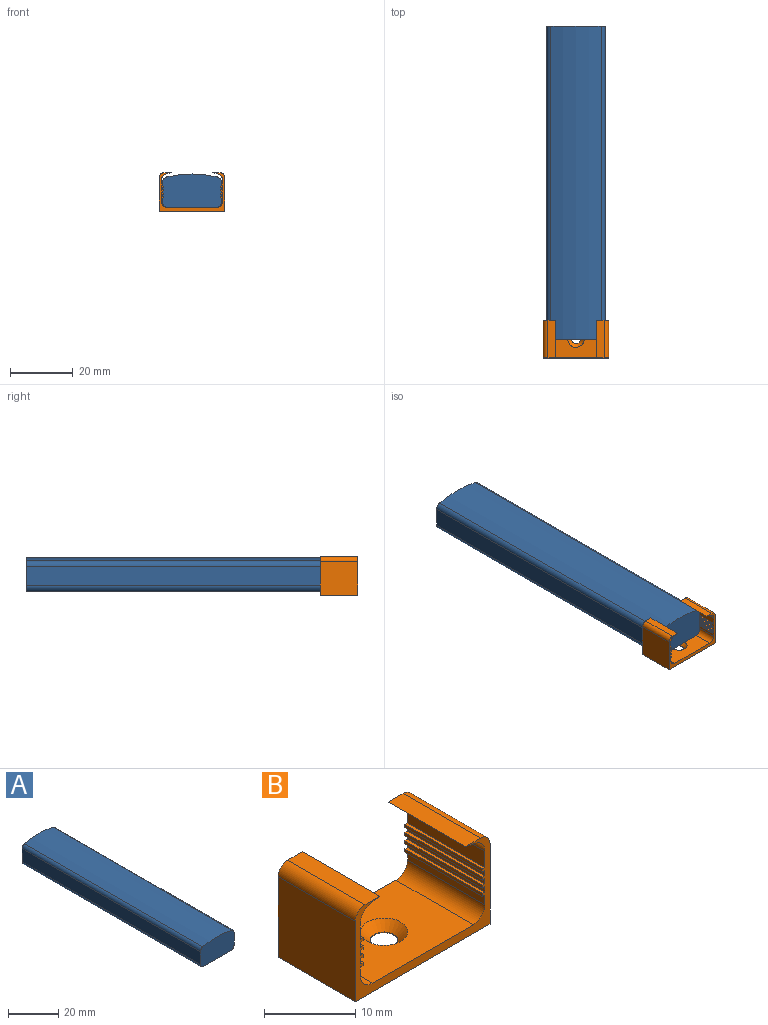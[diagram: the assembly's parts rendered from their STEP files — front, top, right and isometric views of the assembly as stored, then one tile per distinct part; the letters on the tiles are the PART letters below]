
ASSEMBLY  parts=2 mates=1
PART A: 10 faces, bbox 18.8x100x10.7 mm
  f0: cylinder r=34.63mm len=100mm, axis (0,1,0), area 1618mm2, adj f1,f7,f8,f9
  f1: cylinder r=1.8mm len=100mm, axis (0,1,0), area 240.7mm2, adj f0,f2,f8,f9
  f2: plane 100x6.21mm, normal (-1,0,0), area 620.8mm2, adj f1,f3,f8,f9
  f3: cylinder r=1.8mm len=100mm, axis (0,1,0), area 282.7mm2, adj f2,f4,f8,f9
  f4: plane 100x15.2mm, normal (0,0,-1), area 1520mm2, adj f3,f5,f8,f9
  f5: cylinder r=1.8mm len=100mm, axis (0,1,0), area 282.7mm2, adj f4,f6,f8,f9
  f6: plane 100x6.21mm, normal (1,0,0), area 620.8mm2, adj f5,f7,f8,f9
  f7: cylinder r=1.8mm len=100mm, axis (0,1,0), area 240.7mm2, adj f0,f6,f8,f9
  f8: plane 18.8x10.7mm, normal (0,-1,0), area 190.9mm2, adj f0,f1,f2,f3,f4,f5,f6,f7
  f9: plane 18.8x10.7mm, normal (0,1,0), area 190.9mm2, adj f0,f1,f2,f3,f4,f5,f6,f7
PART B: 52 faces, bbox 20.9x12x12.3 mm
  f0: plane 12x0.41mm, normal (1,0,0), area 4.9mm2, adj f1,f47,f48,f49
  f1: plane 12x0.4mm, normal (0,0,1), area 4.8mm2, adj f0,f2,f48,f49
  f2: plane 12x2.2mm, normal (1,0,0), area 26.4mm2, adj f1,f3,f48,f49
  f3: cylinder r=1.8mm len=12mm, axis (0,1,0), area 28.9mm2, adj f2,f4,f48,f49
  f4: cylinder r=36.01mm len=12mm, axis (0,1,0), area 19.8mm2, adj f3,f5,f48,f49
  f5: plane 12x2.3mm, normal (0,0,1), area 27.6mm2, adj f4,f6,f48,f49
  f6: cylinder r=1.5mm len=12mm, axis (0,1,0), area 28.3mm2, adj f5,f7,f48,f49
  f7: plane 12x10.8mm, normal (-1,0,0), area 129.6mm2, adj f6,f8,f48,f49
  f8: plane 20.9x12mm, normal (0,0,-1), area 243.7mm2, adj f7,f9,f48,f49,f50
  f9: plane 12x10.8mm, normal (1,0,0), area 129.6mm2, adj f8,f10,f48,f49
  f10: cylinder r=1.5mm len=12mm, axis (0,1,0), area 28.3mm2, adj f9,f11,f48,f49
  f11: plane 12x2.3mm, normal (0,0,1), area 27.6mm2, adj f10,f12,f48,f49
  f12: cylinder r=36.01mm len=12mm, axis (0,1,0), area 19.8mm2, adj f11,f13,f48,f49
  f13: cylinder r=1.8mm len=12mm, axis (0,1,0), area 28.9mm2, adj f12,f14,f48,f49
  f14: plane 12x2.2mm, normal (-1,0,0), area 26.4mm2, adj f13,f15,f48,f49
  f15: plane 12x0.4mm, normal (0,0,1), area 4.8mm2, adj f14,f16,f48,f49
  f16: plane 12x0.41mm, normal (-1,0,0), area 4.9mm2, adj f15,f17,f48,f49
  f17: plane 12x0.4mm, normal (0,0,-1), area 4.8mm2, adj f16,f18,f48,f49
  f18: plane 12x0.69mm, normal (-1,0,0), area 8.3mm2, adj f17,f19,f48,f49
  f19: plane 12x0.4mm, normal (0,0,1), area 4.8mm2, adj f18,f20,f48,f49
  f20: plane 12x0.41mm, normal (-1,0,0), area 4.9mm2, adj f19,f21,f48,f49
  f21: plane 12x0.4mm, normal (0,0,-1), area 4.8mm2, adj f20,f22,f48,f49
  f22: plane 12x0.69mm, normal (-1,0,0), area 8.3mm2, adj f21,f23,f48,f49
  f23: plane 12x0.4mm, normal (0,0,1), area 4.8mm2, adj f22,f24,f48,f49
  f24: plane 12x0.41mm, normal (-1,0,0), area 4.9mm2, adj f23,f25,f48,f49
  f25: plane 12x0.4mm, normal (0,0,-1), area 4.8mm2, adj f24,f26,f48,f49
  f26: plane 12x0.69mm, normal (-1,0,0), area 8.3mm2, adj f25,f27,f48,f49
  f27: plane 12x0.4mm, normal (0,0,1), area 4.8mm2, adj f26,f28,f48,f49
  f28: plane 12x0.41mm, normal (-1,0,0), area 4.9mm2, adj f27,f29,f48,f49
  f29: plane 12x0.4mm, normal (0,0,-1), area 4.8mm2, adj f28,f30,f48,f49
  f30: plane 12x1.29mm, normal (-1,0,0), area 15.5mm2, adj f29,f31,f48,f49
  f31: cylinder r=1.8mm len=12mm, axis (0,1,0), area 33.9mm2, adj f30,f32,f48,f49
  f32: plane 15.7x12mm, normal (0,0,1), area 167.2mm2, adj f31,f33,f48,f49,f51
  f33: cylinder r=1.8mm len=12mm, axis (0,1,0), area 33.9mm2, adj f32,f34,f48,f49
  f34: plane 12x1.29mm, normal (1,0,0), area 15.5mm2, adj f33,f35,f48,f49
  f35: plane 12x0.4mm, normal (0,0,-1), area 4.8mm2, adj f34,f36,f48,f49
  f36: plane 12x0.41mm, normal (1,0,0), area 4.9mm2, adj f35,f37,f48,f49
  f37: plane 12x0.4mm, normal (0,0,1), area 4.8mm2, adj f36,f38,f48,f49
  f38: plane 12x0.69mm, normal (1,0,0), area 8.3mm2, adj f37,f39,f48,f49
  f39: plane 12x0.4mm, normal (0,0,-1), area 4.8mm2, adj f38,f40,f48,f49
  f40: plane 12x0.41mm, normal (1,0,0), area 4.9mm2, adj f39,f41,f48,f49
  f41: plane 12x0.4mm, normal (0,0,1), area 4.8mm2, adj f40,f42,f48,f49
  f42: plane 12x0.69mm, normal (1,0,0), area 8.3mm2, adj f41,f43,f48,f49
  f43: plane 12x0.4mm, normal (0,0,-1), area 4.8mm2, adj f42,f44,f48,f49
  f44: plane 12x0.41mm, normal (1,0,0), area 4.9mm2, adj f43,f45,f48,f49
  f45: plane 12x0.4mm, normal (0,0,1), area 4.8mm2, adj f44,f46,f48,f49
  f46: plane 12x0.69mm, normal (1,0,0), area 8.3mm2, adj f45,f47,f48,f49
  f47: plane 12x0.4mm, normal (0,0,-1), area 4.8mm2, adj f0,f46,f48,f49
  f48: plane 20.9x12.3mm, normal (0,-1,0), area 47.3mm2, adj f0,f1,f2,f3,f4,f5,f6,f7
  f49: plane 20.9x12.3mm, normal (0,1,0), area 47.3mm2, adj f0,f1,f2,f3,f4,f5,f6,f7
  f50: cylinder r=1.5mm len=3mm, axis (0,0,1), area 0.9mm2, adj f8,f51
  f51: cone r=1.5mm half-angle=45deg, axis (0,0,1), area 20mm2, adj f32,f50
PLACE A t=(-341.85,311.18,-137.83)mm fixed
PLACE B t=(-341.85,211.18,-137.33)mm
MATE fastened B.f51 <-> A.f4  axis (0,0,1) through (-341.85,211.18,-142.53)mm
